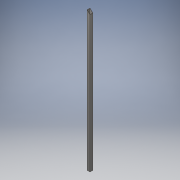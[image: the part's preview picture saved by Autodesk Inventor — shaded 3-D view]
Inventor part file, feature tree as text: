
AUTODESK INVENTOR PART (.ipt)
format: ipt  version: 2019 (Build 230136000, 136)  size: 150,528 bytes
history: native  units: mm
features: extrude x3, sketch x3, projected_geometry x1
ambient origin geometry x8: Origin, YZ Plane, XZ Plane, XY Plane, X Axis, Y Axis, Z Axis, Center Point
bodies: Solid1 (feature_tree)
feature tree (7):
  extrude  "Extrusion1"  Depth=30.0mm
  sketch  "Sketch2"  dims[d2=2.5mm d3=2.5mm]
  extrude  "Extrusion2"  Depth=2.5mm
  extrude  "Extrusion3"  TaperAngle=45.0deg  [1 undecoded]
  sketch  "Sketch3"  dims[d4=1400.0mm d5=0.0mm d6=45.0deg d7=45.0deg d8=0.0mm d9=0.0mm d10=0.0mm d11=0.0mm d12=0.0mm d13=0.0mm d20=450.0mm d21=1000.0mm d22=1220.0mm]
  sketch  "Sketch1"  dims[d0=30.0mm d1=30.0mm]
  projected_geometry  "Projected Loop1"
note: 1 required parameter value undecoded (feature->parameter linkage not recoverable at this tier; creation-order binding heuristic only, values carry confidence <= 0.55)
